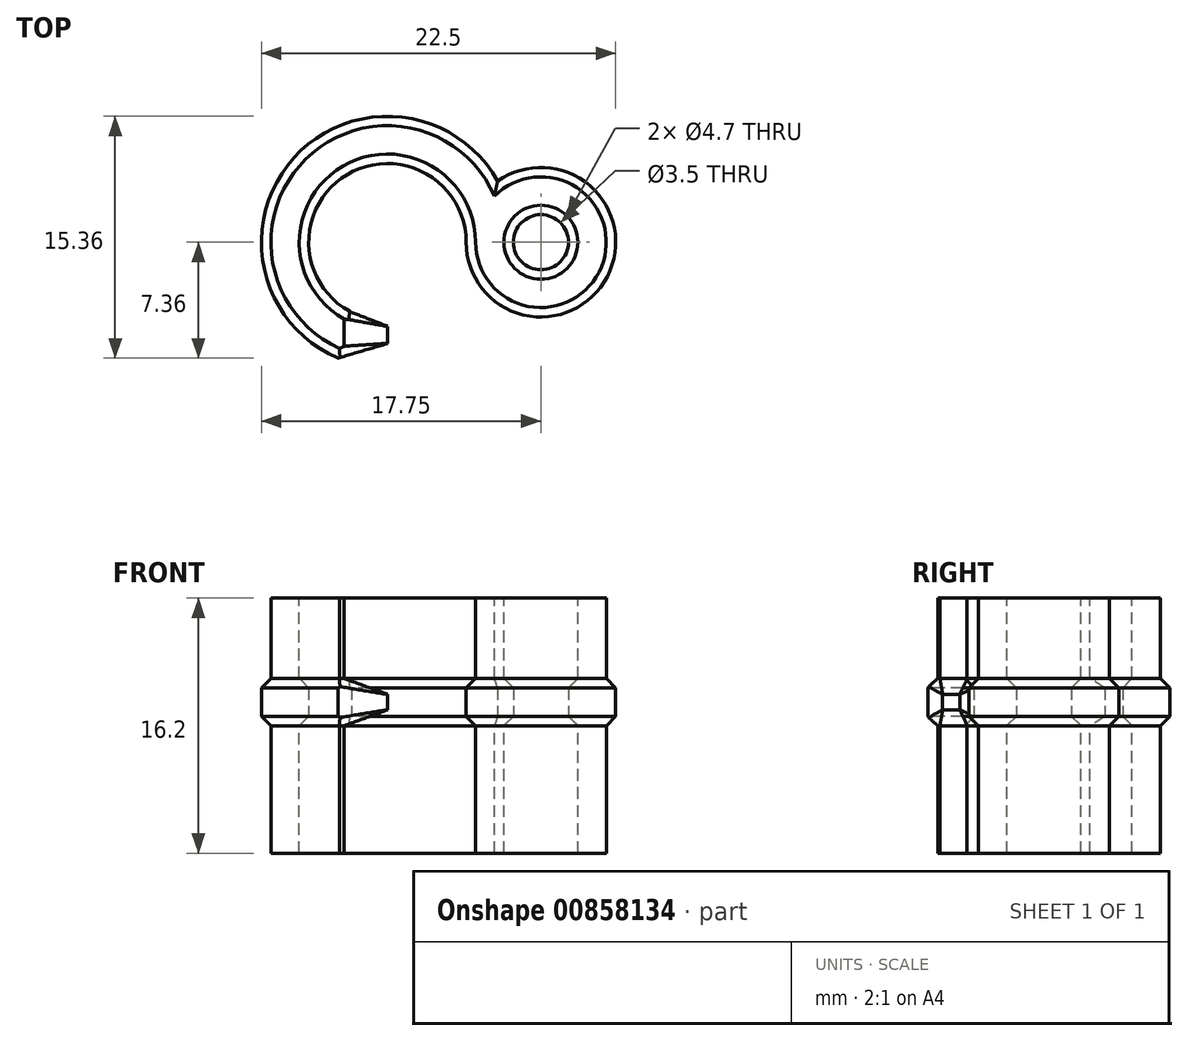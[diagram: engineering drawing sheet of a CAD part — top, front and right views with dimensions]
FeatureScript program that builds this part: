
annotation { "Feature Type Name" : "Feature", "Feature Type Description" : "" }
export const myFeature = defineFeature(function(context is Context, id is Id, definition is map)
    precondition{}
    {
        {
            var Q0;
            Q0=qCreatedBy(makeId("Top.planeOp"),FACE);
            var sketch = newSketch(context, id + "F0", { "sketchPlane" : qUnion([Q0])});
            skCircle(sketch, "E0", {"center": v(0, 0) * mm, "radius": 5 * mm});
            skCircle(sketch, "E1", {"center": v(9.75, 0) * mm, "radius": 1.75 * mm});
            skLineSegment(sketch, "E2", {"start": v(5, 0) * mm, "end": v(8, 0) * mm, "construction": true});
            skCircle(sketch, "E3.0", {"center": v(0, 0) * mm, "radius": 8 * mm});
            skCircle(sketch, "E4.0", {"center": v(9.75, 0) * mm, "radius": 4.75 * mm});
            skLineSegment(sketch, "E5", {"start": v(0, -5) * mm, "end": v(0, -8) * mm});
            skSolve(sketch);
        }
        {
            var Q0;
            {var subQ0=sQuery(id+"F0.wireOp",EDGE,"E5");Q0=makeQuery(id+"F0.imprint","IMPRINT",FACE,{"disambiguationData":[TD([[makeQuery(id+"F0.imprint","IMPRINT",EDGE,{"derivedFrom":subQ0}),-1.0]])]});}
            var Q1;
            {var subQ0=sQuery(id+"F0.wireOp",EDGE,"E3.0");var subQ1=makeQuery(id+"F0.imprint","INTERSECT",VERTEX,{"derivedFrom":[sQuery(id+"F0.wireOp",EDGE,"E1"),subQ0]});Q1=makeQuery(id+"F0.imprint","IMPRINT",FACE,{"disambiguationData":[TD([[makeQuery(id+"F0.imprint","IMPRINT",EDGE,{"disambiguationData":[TD([[subQ1,-1.0]])],"derivedFrom":subQ0}),1.0]])]});}
            var Q2;
            {var subQ0=sQuery(id+"F0.wireOp",EDGE,"E1");Q2=makeQuery(id+"F0.imprint","IMPRINT",FACE,{"disambiguationData":[TD([[makeQuery(id+"F0.imprint","IMPRINT",EDGE,{"derivedFrom":subQ0}),-1.0]])]});}
            extrude(context, id + "F1", {"entities" : qUnion([Q0, Q1, Q2]), "depth" : 3 * mm, "offsetDistance" : 25 * mm});
        }
        {
            var Q0;
            Q0=makeQuery(id+"F1.opExtrude","CAP_EDGE",EDGE,{"disambiguationData":[OSD([sQuery(id+"F0.wireOp",EDGE,"E0")])],"isStart":false});
            var Q1;
            Q1=makeQuery(id+"F1.opExtrude","CAP_EDGE",EDGE,{"disambiguationData":[OSD([sQuery(id+"F0.wireOp",EDGE,"E3.0")])],"isStart":false});
            var Q2;
            Q2=makeQuery(id+"F1.opExtrude","CAP_EDGE",EDGE,{"disambiguationData":[OSD([sQuery(id+"F0.wireOp",EDGE,"E4.0")])],"isStart":false});
            var Q3;
            Q3=makeQuery(id+"F1.opExtrude","CAP_EDGE",EDGE,{"disambiguationData":[OSD([sQuery(id+"F0.wireOp",EDGE,"E1")])],"isStart":false});
            var Q4;
            Q4=makeQuery(id+"F1.opExtrude","CAP_EDGE",EDGE,{"disambiguationData":[OSD([sQuery(id+"F0.wireOp",EDGE,"E4.0")])],"isStart":true});
            var Q5;
            Q5=makeQuery(id+"F1.opExtrude","CAP_EDGE",EDGE,{"disambiguationData":[OSD([sQuery(id+"F0.wireOp",EDGE,"E0")])],"isStart":true});
            var Q6;
            Q6=makeQuery(id+"F1.opExtrude","CAP_EDGE",EDGE,{"disambiguationData":[OSD([sQuery(id+"F0.wireOp",EDGE,"E3.0")])],"isStart":true});
            var Q7;
            Q7=makeQuery(id+"F1.opExtrude","CAP_EDGE",EDGE,{"disambiguationData":[OSD([sQuery(id+"F0.wireOp",EDGE,"E1")])],"isStart":true});
            chamfer(context, id + "F2", {"entities" : qUnion([Q0, Q1, Q2, Q3, Q4, Q5, Q6, Q7]), "width" : 0.6 * mm, "tangentPropagation" : true});
        }
        {
            var Q0;
            Q0=makeQuery(id+"F1.opExtrude","CAP_EDGE",EDGE,{"disambiguationData":[OSD([sQuery(id+"F0.wireOp",EDGE,"E5")])],"isStart":false});
            var Q1;
            Q1=makeQuery(id+"F1.opExtrude","CAP_EDGE",EDGE,{"disambiguationData":[OSD([sQuery(id+"F0.wireOp",EDGE,"E5")])],"isStart":true});
            var Q2;
            Q2=makeQuery(id+"F1.opExtrude","SWEPT_EDGE",EDGE,{"disambiguationData":[OSD([sQuery(id+"F0.wireOp",EDGE,"E0"),sQuery(id+"F0.wireOp",EDGE,"E5")])]});
            var Q3;
            Q3=makeQuery(id+"F1.opExtrude","SWEPT_EDGE",EDGE,{"disambiguationData":[OSD([sQuery(id+"F0.wireOp",EDGE,"E3.0"),sQuery(id+"F0.wireOp",EDGE,"E5")])]});
            var Q4;
            Q4=makeQuery(id+"F2.opChamfer","BLEND_EDGE",EDGE,{"blendedFrom":[makeQuery(id+"F1.opExtrude","CAP_EDGE",EDGE,{"disambiguationData":[OSD([sQuery(id+"F0.wireOp",EDGE,"E3.0")])],"isStart":false}),makeQuery(id+"F1.opExtrude","SWEPT_FACE",FACE,{"disambiguationData":[OSD([sQuery(id+"F0.wireOp",EDGE,"E5")])]})],"blendedInto":[makeQuery(id+"F1.opExtrude","SWEPT_FACE",FACE,{"disambiguationData":[OSD([sQuery(id+"F0.wireOp",EDGE,"E5")])]})]});
            var Q5;
            Q5=makeQuery(id+"F2.opChamfer","BLEND_EDGE",EDGE,{"blendedFrom":[makeQuery(id+"F1.opExtrude","CAP_EDGE",EDGE,{"disambiguationData":[OSD([sQuery(id+"F0.wireOp",EDGE,"E3.0")])],"isStart":true}),makeQuery(id+"F1.opExtrude","SWEPT_FACE",FACE,{"disambiguationData":[OSD([sQuery(id+"F0.wireOp",EDGE,"E5")])]})],"blendedInto":[makeQuery(id+"F1.opExtrude","SWEPT_FACE",FACE,{"disambiguationData":[OSD([sQuery(id+"F0.wireOp",EDGE,"E5")])]})]});
            var Q6;
            Q6=makeQuery(id+"F2.opChamfer","BLEND_EDGE",EDGE,{"blendedFrom":[makeQuery(id+"F1.opExtrude","CAP_EDGE",EDGE,{"disambiguationData":[OSD([sQuery(id+"F0.wireOp",EDGE,"E0")])],"isStart":true}),makeQuery(id+"F1.opExtrude","SWEPT_FACE",FACE,{"disambiguationData":[OSD([sQuery(id+"F0.wireOp",EDGE,"E5")])]})],"blendedInto":[makeQuery(id+"F1.opExtrude","SWEPT_FACE",FACE,{"disambiguationData":[OSD([sQuery(id+"F0.wireOp",EDGE,"E5")])]})]});
            var Q7;
            Q7=makeQuery(id+"F2.opChamfer","BLEND_EDGE",EDGE,{"blendedFrom":[makeQuery(id+"F1.opExtrude","CAP_EDGE",EDGE,{"disambiguationData":[OSD([sQuery(id+"F0.wireOp",EDGE,"E0")])],"isStart":false}),makeQuery(id+"F1.opExtrude","SWEPT_FACE",FACE,{"disambiguationData":[OSD([sQuery(id+"F0.wireOp",EDGE,"E5")])]})],"blendedInto":[makeQuery(id+"F1.opExtrude","SWEPT_FACE",FACE,{"disambiguationData":[OSD([sQuery(id+"F0.wireOp",EDGE,"E5")])]})]});
            chamfer(context, id + "F3", {"entities" : qUnion([Q0, Q1, Q2, Q3, Q4, Q5, Q6, Q7]), "chamferType" : ChamferType.OFFSET_ANGLE, "width" : 1 * mm, "oppositeDirection" : false, "angle" : 70 * degree, "tangentPropagation" : true});
        }
        {
            var Q0;
            Q0=makeQuery(id+"F1.opExtrude","CAP_FACE",FACE,{"disambiguationData":[OSD([sQuery(id+"F0.wireOp",EDGE,"E0"),sQuery(id+"F0.wireOp",EDGE,"E1"),sQuery(id+"F0.wireOp",EDGE,"E3.0"),sQuery(id+"F0.wireOp",EDGE,"E4.0"),sQuery(id+"F0.wireOp",EDGE,"E5")])],"isStart":true});
            extrude(context, id + "F4", {"entities" : qUnion([Q0]), "operationType" : NewBodyOperationType.ADD, "endBound" : BoundingType.SYMMETRIC, "depth" : 16.2 * mm, "offsetDistance" : 25 * mm});
        }
    });
